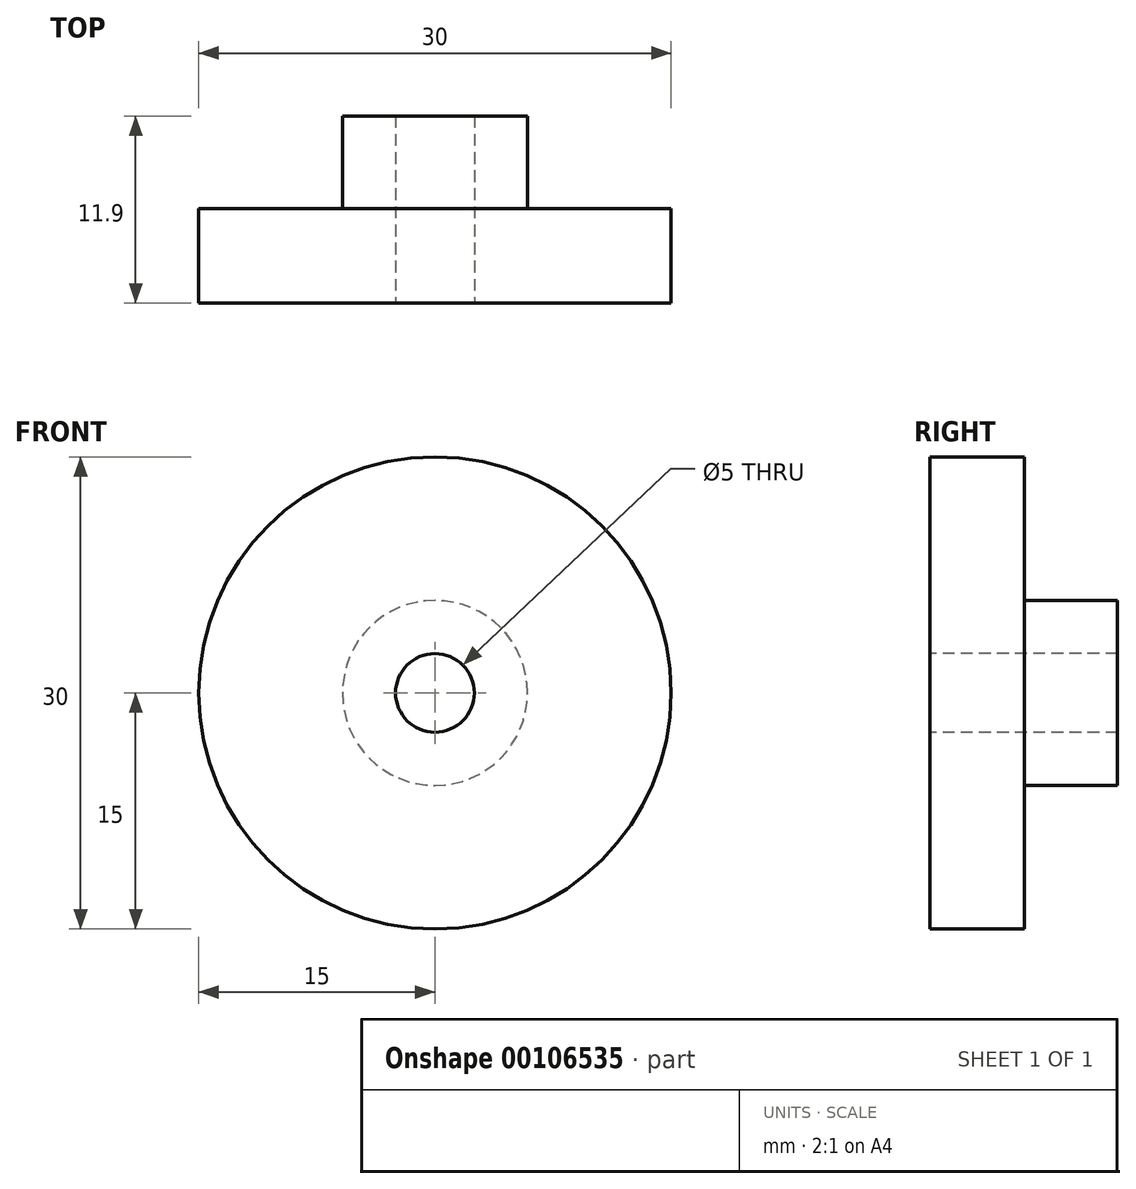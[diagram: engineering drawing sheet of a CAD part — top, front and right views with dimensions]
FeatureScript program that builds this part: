
annotation { "Feature Type Name" : "Feature", "Feature Type Description" : "" }
export const myFeature = defineFeature(function(context is Context, id is Id, definition is map)
    precondition{}
    {
        {
            var Q0;
            Q0=qCreatedBy(makeId("Front.planeOp"),FACE);
            var sketch = newSketch(context, id + "F0", { "sketchPlane" : qUnion([Q0])});
            skCircle(sketch, "E0", {"center": v(0, 0) * mm, "radius": 5.88 * mm});
            skCircle(sketch, "E1", {"center": v(0, 0) * mm, "radius": 15 * mm});
            skCircle(sketch, "E2", {"center": v(0, 0) * mm, "radius": 2.5 * mm});
            skSolve(sketch);
        }
        {
            var Q0;
            Q0=makeQuery(id+"F0.imprint","IMPRINT",FACE,{"disambiguationData":[TD([[makeQuery(id+"F0.imprint","IMPRINT",EDGE,{"derivedFrom":sQuery(id+"F0.wireOp",EDGE,"E0")}),1.0]])]});
            extrude(context, id + "F1", {"entities" : qUnion([Q0]), "oppositeDirection" : true, "depth" : 11.9 * mm});
        }
        {
            var Q0;
            Q0=makeQuery(id+"F0.imprint","IMPRINT",FACE,{"disambiguationData":[TD([[makeQuery(id+"F0.imprint","IMPRINT",EDGE,{"derivedFrom":sQuery(id+"F0.wireOp",EDGE,"E0")}),-1.0]])]});
            extrude(context, id + "F2", {"entities" : qUnion([Q0]), "operationType" : NewBodyOperationType.ADD, "oppositeDirection" : true, "depth" : 6 * mm});
        }
    });
